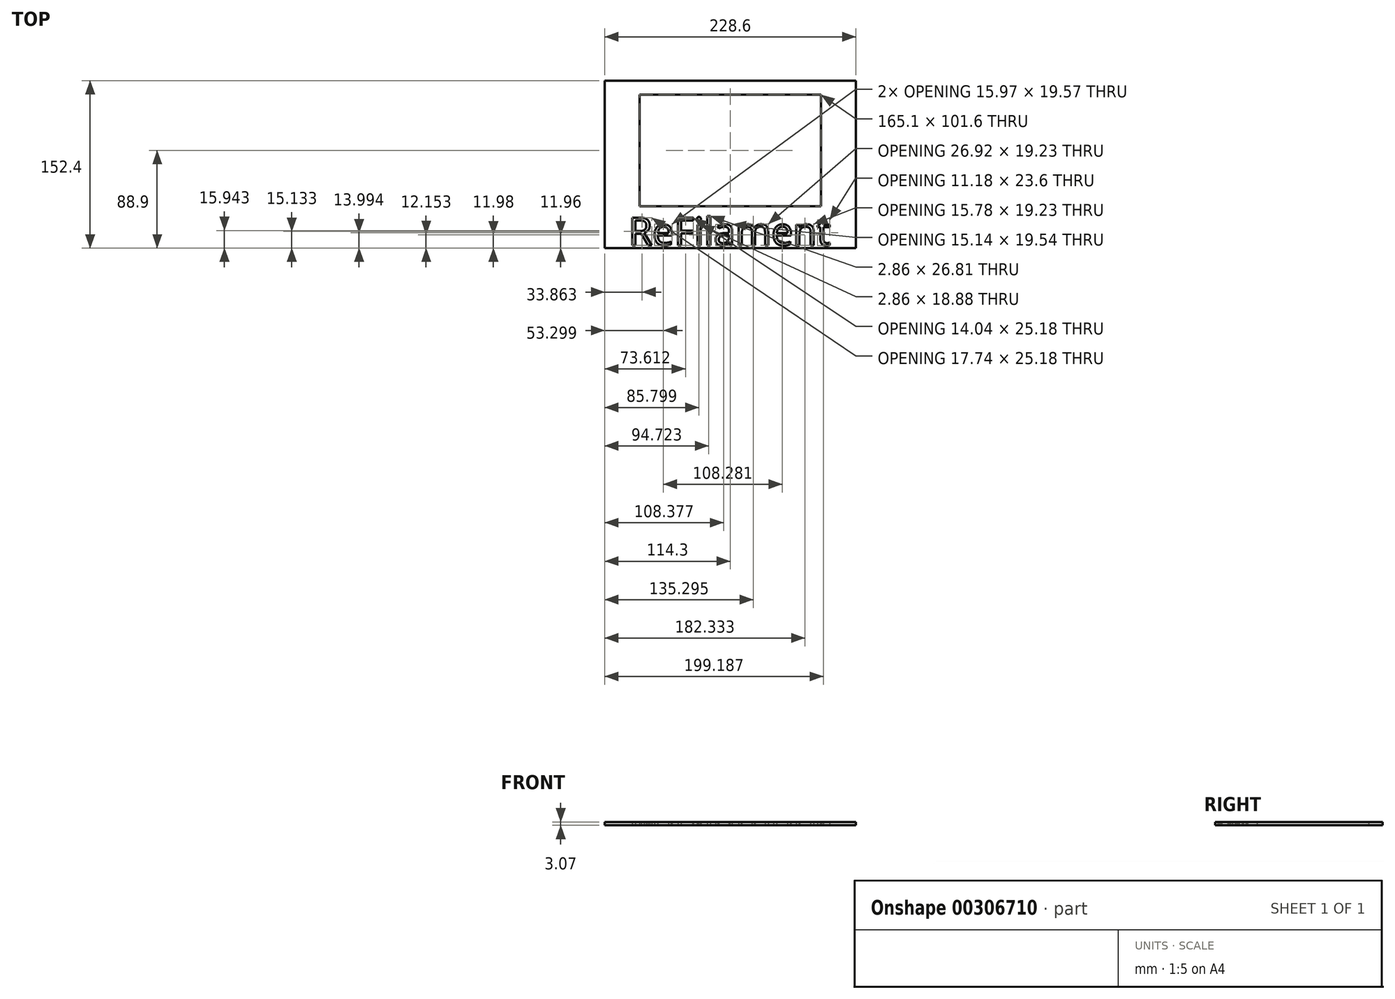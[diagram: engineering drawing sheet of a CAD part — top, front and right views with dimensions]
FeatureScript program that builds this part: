
annotation { "Feature Type Name" : "Feature", "Feature Type Description" : "" }
export const myFeature = defineFeature(function(context is Context, id is Id, definition is map)
    precondition{}
    {
        {
            var Q0;
            Q0=qCreatedBy(makeId("Top.planeOp"),FACE);
            var sketch = newSketch(context, id + "F0", { "sketchPlane" : qUnion([Q0])});
            skLineSegment(sketch, "E0.bottom", {"start": v(114.3, 76.2) * mm, "end": v(-114.3, 76.2) * mm});
            skLineSegment(sketch, "E0.top", {"start": v(114.3, -76.2) * mm, "end": v(-114.3, -76.2) * mm});
            skLineSegment(sketch, "E0.left", {"start": v(114.3, 76.2) * mm, "end": v(114.3, -76.2) * mm});
            skLineSegment(sketch, "E0.right", {"start": v(-114.3, 76.2) * mm, "end": v(-114.3, -76.2) * mm});
            skPoint(sketch, "E0.middle", {"position": v(0, 0) * mm});
            skLineSegment(sketch, "E1.bottom", {"start": v(-82.55, 63.5) * mm, "end": v(82.55, 63.5) * mm});
            skLineSegment(sketch, "E1.top", {"start": v(-82.55, -38.1) * mm, "end": v(82.55, -38.1) * mm});
            skLineSegment(sketch, "E1.left", {"start": v(-82.55, 63.5) * mm, "end": v(-82.55, -38.1) * mm});
            skLineSegment(sketch, "E1.right", {"start": v(82.55, 63.5) * mm, "end": v(82.55, -38.1) * mm});
            skText(sketch, "E2", { "text": "ReFilament", "fontName": "OpenSans-Regular.ttf"});
            const initialGuessF0  = {"E2": [-0.09277, -0.07366, 1, 0, 0.0254]};
            skSetInitialGuess(sketch, initialGuessF0);
            skSolve(sketch);
        }
        {
            var Q0;
            Q0=makeQuery(id+"F0.imprint","IMPRINT",FACE,{"disambiguationData":[TD([[makeQuery(id+"F0.imprint","IMPRINT",EDGE,{"derivedFrom":sQuery(id+"F0.wireOp",EDGE,"E2.sketch_text.stroke-11")}),1.0]])]});
            var Q1;
            Q1=makeQuery(id+"F0.imprint","IMPRINT",FACE,{"disambiguationData":[TD([[makeQuery(id+"F0.imprint","IMPRINT",EDGE,{"derivedFrom":sQuery(id+"F0.wireOp",EDGE,"E2.sketch_text.stroke-32")}),1.0]])]});
            var Q2;
            Q2=makeQuery(id+"F0.imprint","IMPRINT",FACE,{"disambiguationData":[TD([[makeQuery(id+"F0.imprint","IMPRINT",EDGE,{"derivedFrom":sQuery(id+"F0.wireOp",EDGE,"E2.sketch_text.stroke-82")}),1.0]])]});
            var Q3;
            Q3=makeQuery(id+"F0.imprint","IMPRINT",FACE,{"disambiguationData":[TD([[makeQuery(id+"F0.imprint","IMPRINT",EDGE,{"derivedFrom":sQuery(id+"F0.wireOp",EDGE,"E2.sketch_text.stroke-132")}),1.0]])]});
            var Q4;
            Q4=makeQuery(id+"F0.imprint","IMPRINT",FACE,{"disambiguationData":[TD([[makeQuery(id+"F0.imprint","IMPRINT",EDGE,{"derivedFrom":sQuery(id+"F0.wireOp",EDGE,"E0.bottom")}),1.0]])]});
            extrude(context, id + "F1", {"entities" : qUnion([Q0, Q1, Q2, Q3, Q4]), "depth" : 3.07 * mm});
        }
    });
